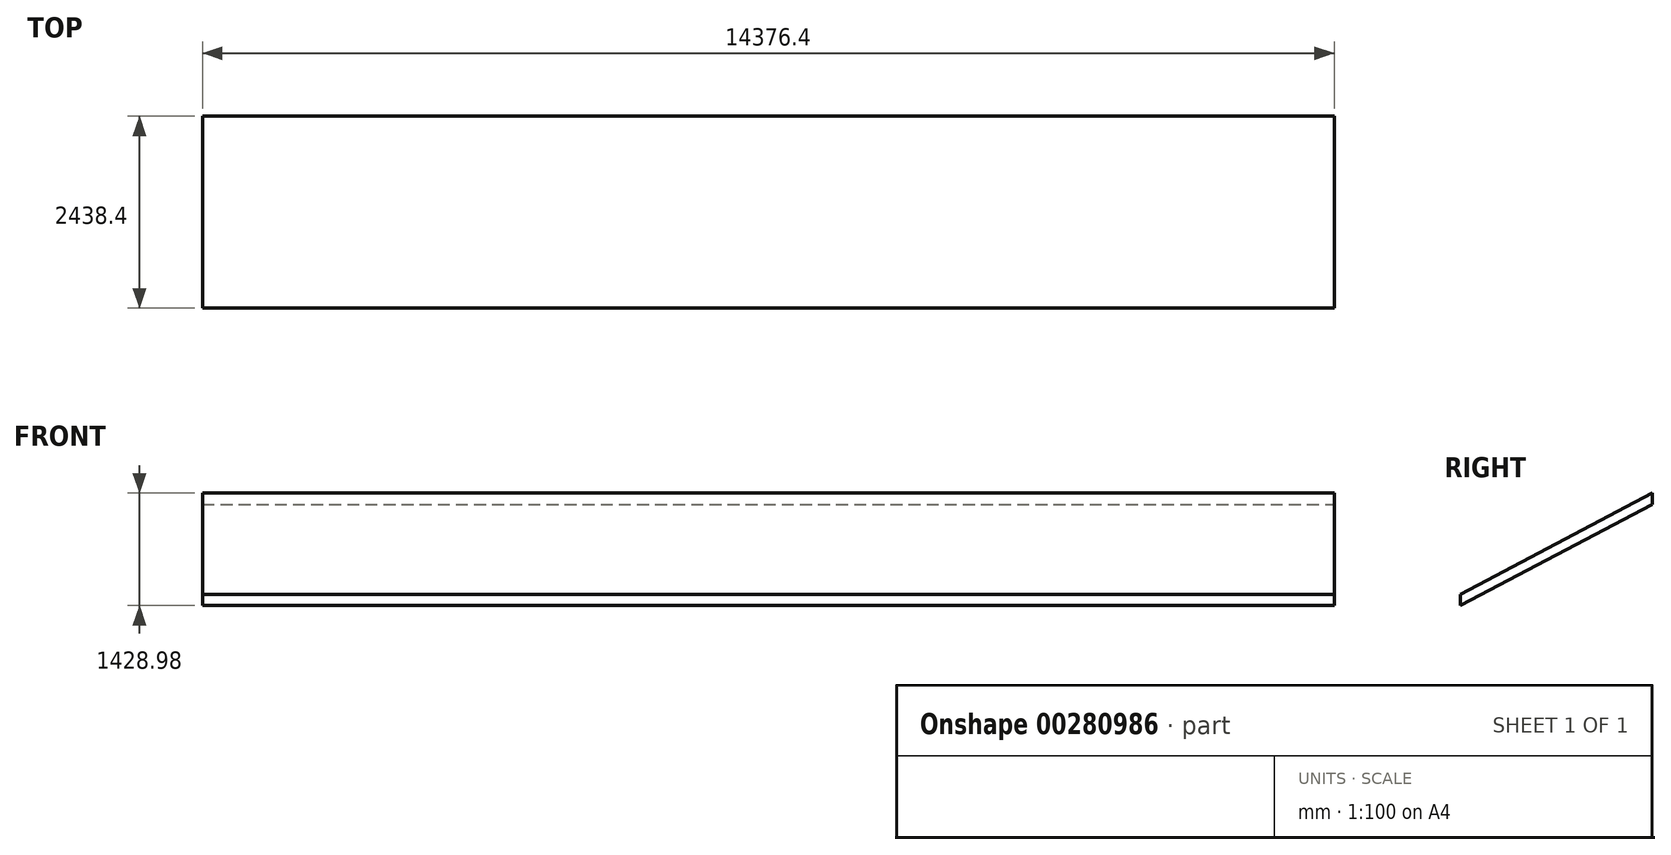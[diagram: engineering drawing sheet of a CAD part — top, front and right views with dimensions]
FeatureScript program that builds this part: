
annotation { "Feature Type Name" : "Feature", "Feature Type Description" : "" }
export const myFeature = defineFeature(function(context is Context, id is Id, definition is map)
    precondition{}
    {
        {
            var Q0;
            Q0=qCreatedBy(makeId("Right.planeOp"),FACE);
            cPlane(context, id + "F0", {"entities" : qUnion([Q0]), "cplaneType" : CPlaneType.OFFSET, "offset" : 6248.4 * mm, "width" : 152.4 * mm, "height" : 152.4 * mm});
        }
        {
            var Q0;
            Q0=qCreatedBy(makeId("Right.planeOp"),FACE);
            cPlane(context, id + "F1", {"entities" : qUnion([Q0]), "cplaneType" : CPlaneType.OFFSET, "offset" : 7670.8 * mm, "oppositeDirection" : true, "width" : 152.4 * mm, "height" : 152.4 * mm});
        }
        {
            var Q0;
            Q0=qCreatedBy(makeId("Right.planeOp"),FACE);
            cPlane(context, id + "F2", {"entities" : qUnion([Q0]), "cplaneType" : CPlaneType.OFFSET, "offset" : 6705.6 * mm, "width" : 152.4 * mm, "height" : 152.4 * mm});
        }
        {
            var Q0;
            Q0=qCreatedBy(id+"F2.planeOp",FACE);
            var sketch = newSketch(context, id + "F3", { "sketchPlane" : qUnion([Q0])});
            skLineSegment(sketch, "E0.MirrorCS", {"start": v(1219.2, 4254.05) * mm, "end": v(-1219.2, 2968.64) * mm});
            skLineSegment(sketch, "E1.0", {"start": v(-1219.2, 2968.64) * mm, "end": v(-1219.2, 3112.2) * mm});
            skPoint(sketch, "E2.orphan", {"position": v(-635, 3276.6) * mm});
            skPoint(sketch, "E3.orphan", {"position": v(7315.2, 3276.6) * mm});
            skLineSegment(sketch, "E4.0", {"start": v(1219.2, 4397.62) * mm, "end": v(-1219.2, 3112.2) * mm});
            skLineSegment(sketch, "E5.0", {"start": v(1219.2, 4254.05) * mm, "end": v(1219.2, 4397.62) * mm});
            skSolve(sketch);
        }
        {
            var Q0;
            Q0=qCreatedBy(makeId("Right.planeOp"),FACE);
            cPlane(context, id + "F4", {"entities" : qUnion([Q0]), "cplaneType" : CPlaneType.OFFSET, "offset" : 8128 * mm, "oppositeDirection" : true, "width" : 152.4 * mm, "height" : 152.4 * mm});
        }
        {
            var Q0;
            Q0=makeQuery(id+"F3.imprint","IMPRINT",FACE,{"disambiguationData":[TD([[makeQuery(id+"F3.imprint","IMPRINT",EDGE,{"derivedFrom":sQuery(id+"F3.wireOp",EDGE,"E0.MirrorCS")}),-1.0]])]});
            extrude(context, id + "F5", {"entities" : qUnion([Q0]), "oppositeDirection" : true, "depth" : 14376.4 * mm});
        }
    });
